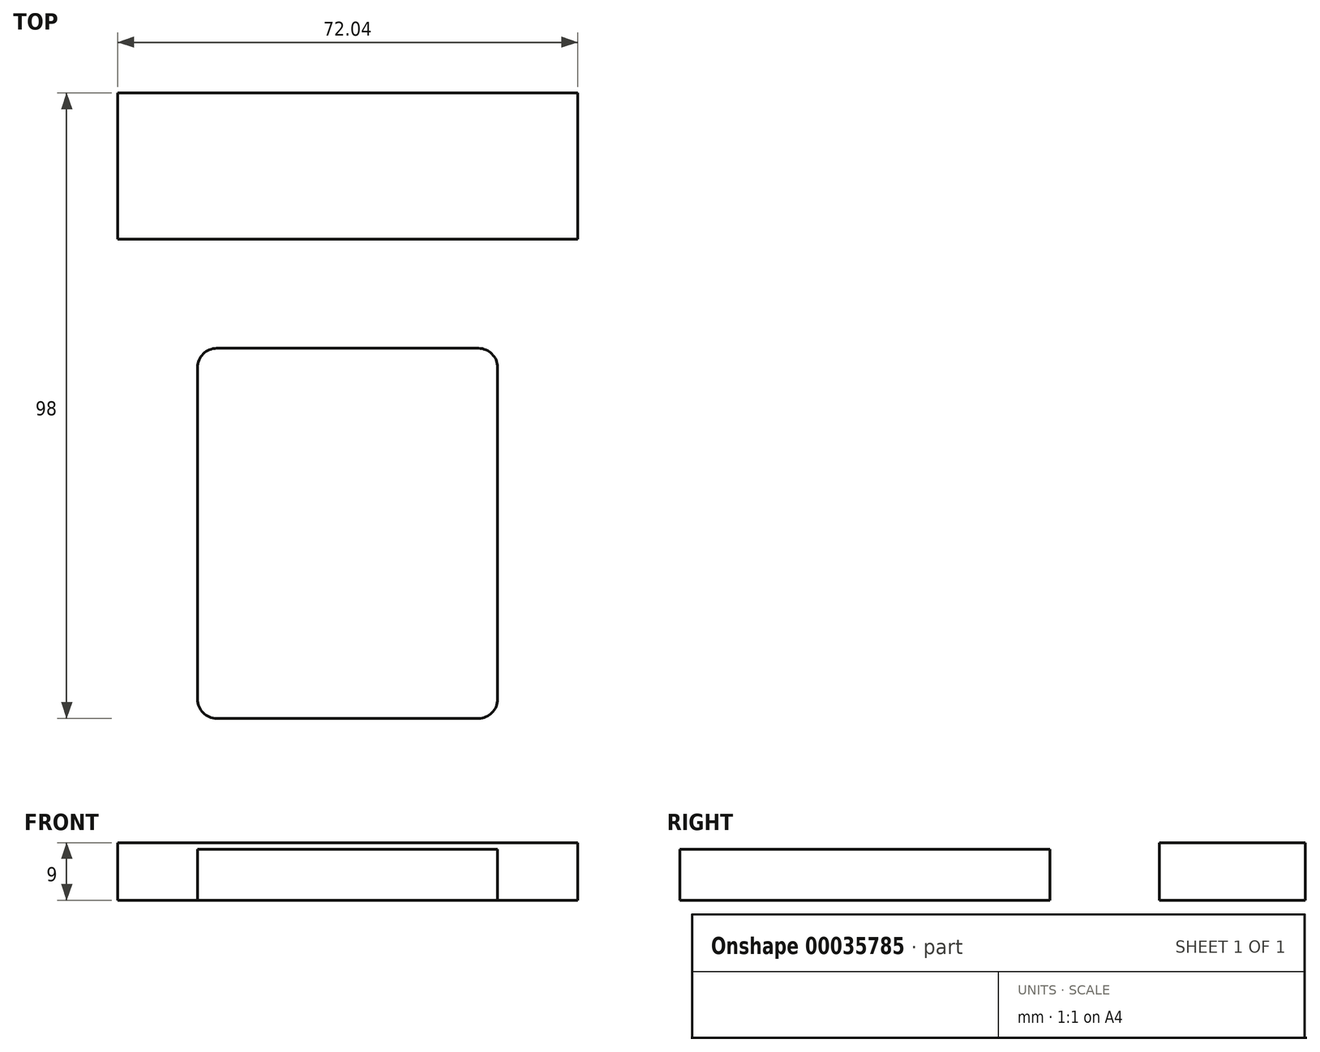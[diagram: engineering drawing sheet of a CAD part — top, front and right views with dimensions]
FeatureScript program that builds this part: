
annotation { "Feature Type Name" : "Feature", "Feature Type Description" : "" }
export const myFeature = defineFeature(function(context is Context, id is Id, definition is map)
    precondition{}
    {
        {
            var Q0;
            Q0=qCreatedBy(makeId("Top.planeOp"),FACE);
            var sketch = newSketch(context, id + "F0", { "sketchPlane" : qUnion([Q0])});
            skLineSegment(sketch, "E0", {"start": v(0, 0) * mm, "end": v(0, 58) * mm, "construction": true});
            skLineSegment(sketch, "E1", {"start": v(0, 0) * mm, "end": v(-23.5, 0) * mm, "construction": true});
            skLineSegment(sketch, "E2", {"start": v(0, 0) * mm, "end": v(23.5, 0) * mm, "construction": true});
            skLineSegment(sketch, "E3.bottom", {"start": v(-23.5, 58) * mm, "end": v(23.5, 58) * mm});
            skLineSegment(sketch, "E3.top", {"start": v(-23.5, 0) * mm, "end": v(23.5, 0) * mm});
            skLineSegment(sketch, "E3.left", {"start": v(-23.5, 58) * mm, "end": v(-23.5, 0) * mm});
            skLineSegment(sketch, "E3.right", {"start": v(23.5, 58) * mm, "end": v(23.5, 0) * mm});
            skLineSegment(sketch, "E4", {"start": v(0, 58) * mm, "end": v(0, 68) * mm, "construction": true});
            skSolve(sketch);
        }
        {
            var Q0;
            Q0=qCreatedBy(makeId("Top.planeOp"),FACE);
            var sketch = newSketch(context, id + "F1", { "sketchPlane" : qUnion([Q0])});
            skLineSegment(sketch, "E5.bottom", {"start": v(-40, 104) * mm, "end": v(40, 104) * mm, "construction": true});
            skLineSegment(sketch, "E5.left", {"start": v(-40, 104) * mm, "end": v(-40, 68) * mm, "construction": true});
            skPoint(sketch, "E6.endSnap0", {"position": v(0, 104) * mm});
            skLineSegment(sketch, "E7.bottom", {"start": v(-40, 104) * mm, "end": v(-36, 104) * mm, "construction": true});
            skLineSegment(sketch, "E7.top", {"start": v(-40, 68) * mm, "end": v(-36, 68) * mm, "construction": true});
            skLineSegment(sketch, "E7.right", {"start": v(-36, 104) * mm, "end": v(-36, 68) * mm, "construction": true});
            skLineSegment(sketch, "E8.top", {"start": v(-40, 98) * mm, "end": v(40.04, 98) * mm, "construction": true});
            skLineSegment(sketch, "E8.left", {"start": v(-40, 104) * mm, "end": v(-40, 98) * mm, "construction": true});
            skLineSegment(sketch, "E8.right", {"start": v(40.04, 104) * mm, "end": v(40.04, 98) * mm, "construction": true});
            skLineSegment(sketch, "E9.bottom", {"start": v(40, 104) * mm, "end": v(36.04, 104) * mm, "construction": true});
            skLineSegment(sketch, "E9.top", {"start": v(40, 68) * mm, "end": v(36.04, 68) * mm, "construction": true});
            skLineSegment(sketch, "E9.left", {"start": v(40, 104) * mm, "end": v(40, 68) * mm, "construction": true});
            skLineSegment(sketch, "E9.right", {"start": v(36.04, 104) * mm, "end": v(36.04, 68) * mm, "construction": true});
            skLineSegment(sketch, "E10.bottom", {"start": v(-40, 68) * mm, "end": v(40, 68) * mm, "construction": true});
            skLineSegment(sketch, "E10.top", {"start": v(-40, 75.11) * mm, "end": v(40, 75.11) * mm, "construction": true});
            skLineSegment(sketch, "E10.left", {"start": v(-40, 68) * mm, "end": v(-40, 75.11) * mm, "construction": true});
            skLineSegment(sketch, "E10.right", {"start": v(40, 68) * mm, "end": v(40, 75.11) * mm, "construction": true});
            skLineSegment(sketch, "E11", {"start": v(-36, 98) * mm, "end": v(-36, 75.11) * mm});
            skLineSegment(sketch, "E12", {"start": v(-36, 75.11) * mm, "end": v(36.04, 75.11) * mm});
            skLineSegment(sketch, "E13", {"start": v(36.04, 75.11) * mm, "end": v(36.04, 98) * mm});
            skLineSegment(sketch, "E14", {"start": v(36.04, 98) * mm, "end": v(-36, 98) * mm});
            skSolve(sketch);
        }
        {
            var Q0;
            Q0=makeQuery(id+"F0.imprint","IMPRINT",FACE,{"disambiguationData":[TD([[makeQuery(id+"F0.imprint","IMPRINT",EDGE,{"derivedFrom":sQuery(id+"F0.wireOp",EDGE,"E3.bottom")}),-1.0]])]});
            extrude(context, id + "F2", {"entities" : qUnion([Q0]), "depth" : 8 * mm});
        }
        {
            var Q0;
            Q0=makeQuery(id+"F1.imprint","IMPRINT",FACE,{"disambiguationData":[TD([[makeQuery(id+"F1.imprint","IMPRINT",EDGE,{"derivedFrom":sQuery(id+"F1.wireOp",EDGE,"E11")}),1.0]])]});
            extrude(context, id + "F3", {"entities" : qUnion([Q0]), "depth" : 9 * mm});
        }
        {
            var Q0;
            Q0=makeQuery(id+"F2.opExtrude","SWEPT_EDGE",EDGE,{"disambiguationData":[OSD([sQuery(id+"F0.wireOp",EDGE,"E3.bottom"),sQuery(id+"F0.wireOp",EDGE,"E3.left")])]});
            var Q1;
            Q1=makeQuery(id+"F2.opExtrude","SWEPT_EDGE",EDGE,{"disambiguationData":[OSD([sQuery(id+"F0.wireOp",EDGE,"E3.bottom"),sQuery(id+"F0.wireOp",EDGE,"E3.right")])]});
            var Q2;
            Q2=makeQuery(id+"F2.opExtrude","SWEPT_EDGE",EDGE,{"disambiguationData":[OSD([sQuery(id+"F0.wireOp",EDGE,"E3.top"),sQuery(id+"F0.wireOp",EDGE,"E3.right")])]});
            var Q3;
            Q3=makeQuery(id+"F2.opExtrude","SWEPT_EDGE",EDGE,{"disambiguationData":[OSD([sQuery(id+"F0.wireOp",EDGE,"E3.top"),sQuery(id+"F0.wireOp",EDGE,"E3.left")])]});
            fillet(context, id + "F4", {"entities" : qUnion([Q0, Q1, Q2, Q3]), "radius" : 3 * mm, "tangentPropagation" : true, "allowEdgeOverflow" : false});
        }
    });
